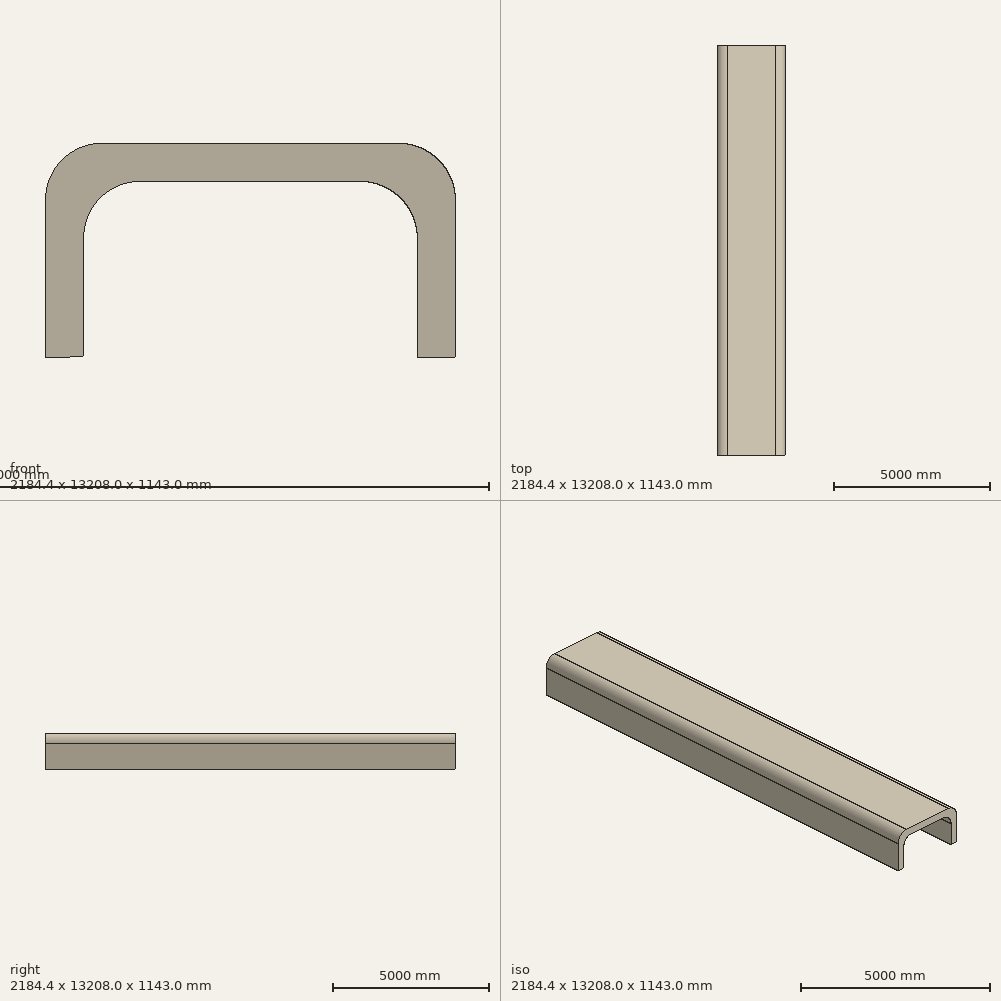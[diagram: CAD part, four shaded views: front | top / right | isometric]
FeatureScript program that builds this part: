
annotation { "Feature Type Name" : "Feature", "Feature Type Description" : "" }
export const myFeature = defineFeature(function(context is Context, id is Id, definition is map)
    precondition{}
    {
        {
            var Q0;
            Q0=qCreatedBy(makeId("Front.planeOp"),FACE);
            var sketch = newSketch(context, id + "F0", { "sketchPlane" : qUnion([Q0])});
            skLineSegment(sketch, "E0", {"start": v(-13991.15, 0) * mm, "end": v(-13991.15, 1143) * mm});
            skLineSegment(sketch, "E1", {"start": v(-13991.15, 1143) * mm, "end": v(-11806.75, 1143) * mm});
            skLineSegment(sketch, "E2", {"start": v(-11806.75, 1143) * mm, "end": v(-11806.75, 0) * mm});
            skLineSegment(sketch, "E3", {"start": v(-11806.75, 0) * mm, "end": v(-12009.95, 0) * mm});
            skLineSegment(sketch, "E4", {"start": v(-12009.95, 0) * mm, "end": v(-12009.95, 939.8) * mm});
            skLineSegment(sketch, "E5", {"start": v(-12009.95, 939.8) * mm, "end": v(-13788.05, 939.8) * mm});
            skLineSegment(sketch, "E6", {"start": v(-13788.05, 939.8) * mm, "end": v(-13788.05, 6.39) * mm});
            skLineSegment(sketch, "E7", {"start": v(-13788.05, 6.39) * mm, "end": v(-13991.15, 0) * mm});
            skSolve(sketch);
        }
        {
            var Q0;
            Q0=makeQuery(id+"F0.imprint","IMPRINT",FACE,{"disambiguationData":[TD([[makeQuery(id+"F0.imprint","IMPRINT",EDGE,{"derivedFrom":sQuery(id+"F0.wireOp",EDGE,"E0")}),-1.0]])]});
            extrude(context, id + "F1", {"entities" : qUnion([Q0]), "depth" : 13208 * mm});
        }
        {
            var Q0;
            Q0=makeQuery(id+"F1.opExtrude","SWEPT_EDGE",EDGE,{"disambiguationData":[OSD([sQuery(id+"F0.wireOp",EDGE,"E1"),sQuery(id+"F0.wireOp",EDGE,"E2")])]});
            var Q1;
            Q1=makeQuery(id+"F1.opExtrude","SWEPT_EDGE",EDGE,{"disambiguationData":[OSD([sQuery(id+"F0.wireOp",EDGE,"E0"),sQuery(id+"F0.wireOp",EDGE,"E1")])]});
            var Q2;
            Q2=makeQuery(id+"F1.opExtrude","SWEPT_EDGE",EDGE,{"disambiguationData":[OSD([sQuery(id+"F0.wireOp",EDGE,"E5"),sQuery(id+"F0.wireOp",EDGE,"E6")])]});
            var Q3;
            Q3=makeQuery(id+"F1.opExtrude","SWEPT_EDGE",EDGE,{"disambiguationData":[OSD([sQuery(id+"F0.wireOp",EDGE,"E4"),sQuery(id+"F0.wireOp",EDGE,"E5")])]});
            fillet(context, id + "F2", {"entities" : qUnion([Q0, Q1, Q2, Q3]), "radius" : 304.8 * mm, "tangentPropagation" : true, "allowEdgeOverflow" : false});
        }
    });
